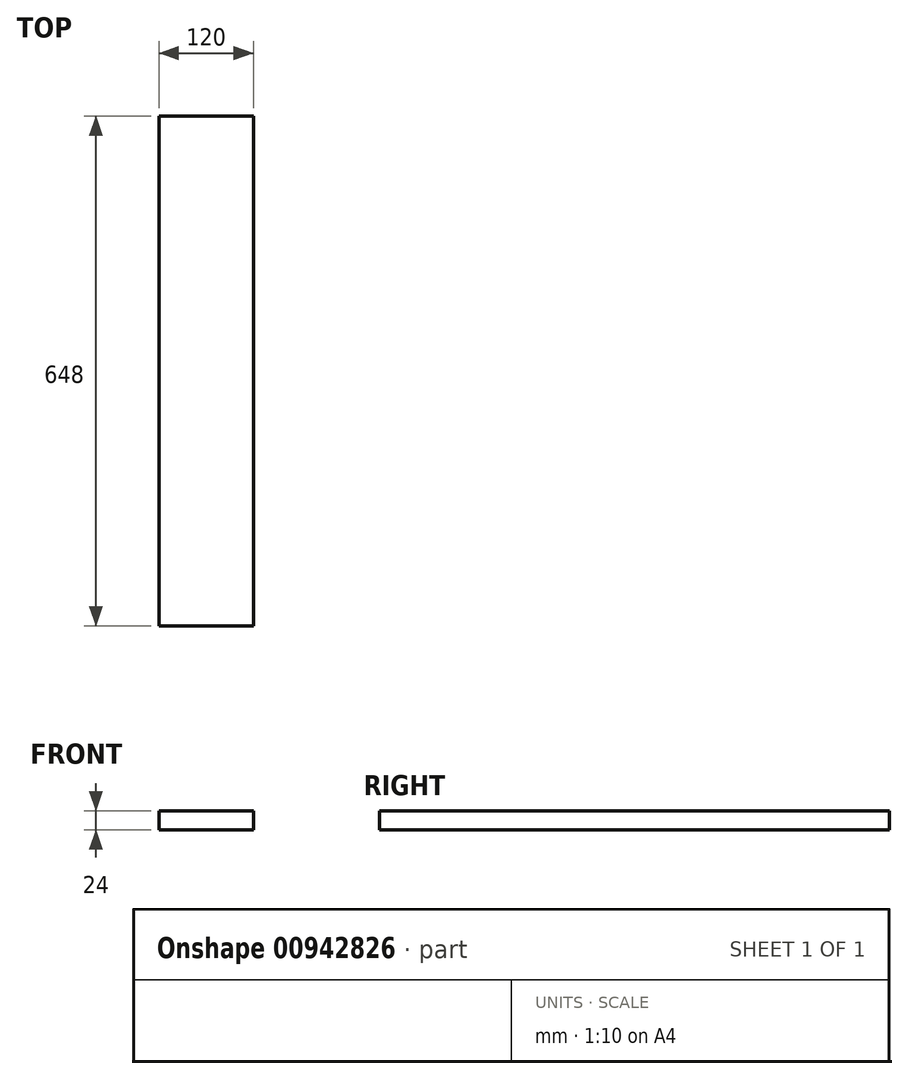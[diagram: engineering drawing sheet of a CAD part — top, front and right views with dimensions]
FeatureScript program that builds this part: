
annotation { "Feature Type Name" : "Feature", "Feature Type Description" : "" }
export const myFeature = defineFeature(function(context is Context, id is Id, definition is map)
    precondition{}
    {
        {
            var Q0;
            Q0=qCreatedBy(makeId("Top.planeOp"),FACE);
            var sketch = newSketch(context, id + "F0", { "sketchPlane" : qUnion([Q0])});
            skLineSegment(sketch, "E0.bottom", {"start": v(-214.21, 326.8) * mm, "end": v(-94.21, 326.8) * mm});
            skLineSegment(sketch, "E0.top", {"start": v(-214.21, -321.2) * mm, "end": v(-94.21, -321.2) * mm});
            skLineSegment(sketch, "E0.left", {"start": v(-214.21, 326.8) * mm, "end": v(-214.21, -321.2) * mm});
            skLineSegment(sketch, "E0.right", {"start": v(-94.21, 326.8) * mm, "end": v(-94.21, -321.2) * mm});
            skSolve(sketch);
        }
        {
            var Q0;
            Q0=makeQuery(id+"F0.imprint","IMPRINT",FACE,{"disambiguationData":[TD([[makeQuery(id+"F0.imprint","IMPRINT",EDGE,{"derivedFrom":sQuery(id+"F0.wireOp",EDGE,"E0.bottom")}),-1.0]])]});
            extrude(context, id + "F1", {"entities" : qUnion([Q0]), "depth" : 24 * mm, "offsetDistance" : 25 * mm});
        }
    });
